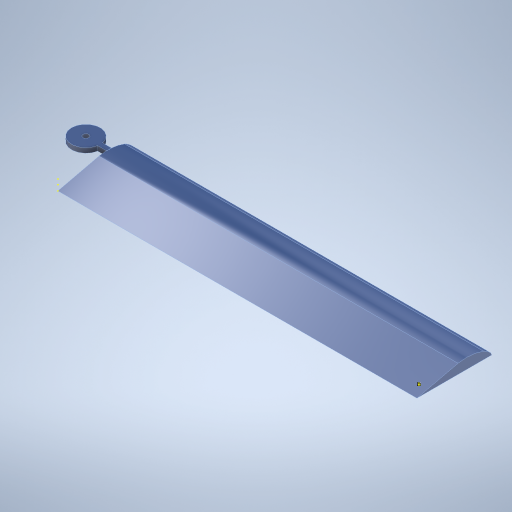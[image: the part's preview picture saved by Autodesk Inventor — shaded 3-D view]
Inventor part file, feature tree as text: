
AUTODESK INVENTOR PART (.ipt)
format: ipt  version: 2023 (Build 270158000, 158)  size: 292,864 bytes
history: native  units: mm
features: sketch x8, extrude x4
ambient origin geometry x8: Origin, YZ Plane, XZ Plane, XY Plane, X Axis, Y Axis, Z Axis, Center Point
bodies: Solid1 (feature_tree)
feature tree (12):
  extrude  "Extrusion1"  Depth=600.0mm TaperAngle=0.0deg
  extrude  "Extrusion2"  Depth=8.0mm
  sketch  "Sketch3"  dims[d5=48.0mm d6=0.0mm d7=39.0mm]
  sketch  "Sketch4"  dims[d8=4.0mm d9=48.0mm]
  extrude  "Extrusion3"  Depth=39.0mm
  sketch  "Sketch6"  dims[d12=10.0mm]
  sketch  "Sketch7"  dims[d13=39.0mm]
  extrude  "Extrusion4"  Depth=48.0mm
  sketch  "Sketch1"  dims[d0=125.0mm d1=600.0mm d2=0.0mm]
  sketch  "Sketch2"  dims[d3=8.0mm d4=8.0mm]
  sketch  "Sketch5"  dims[d10=8.0mm d11=0.0mm]
  sketch  "Sketch8"  dims[d14=4.0mm d15=10.0mm d16=8.0mm d17=0.0mm]
